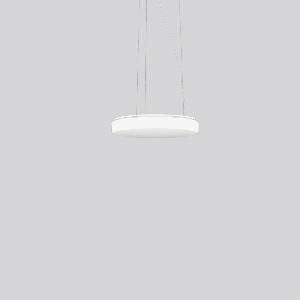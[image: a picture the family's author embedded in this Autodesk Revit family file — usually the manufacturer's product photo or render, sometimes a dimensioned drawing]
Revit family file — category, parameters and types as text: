
# Revit family: flat_polymero_kreis_slim_312089_002_4_338b
name_source: partatom
category: Lighting Fixtures
units: mm (PartAtom-declared; Revit-internal decimal feet)

## family parameters
Cut with Voids When Loaded = No
Host = Face
Light Source = No
Part Type = Normal
Room Calculation Point = No
Round Connector Dimension = Use Diameter
Shared = No

## types (1)
- FLAT POLYMERO KREIS SLIM (1 x LED Modul 840, 2050 lm, 4000)
    Apparent Load = 19 VA
    CIE Flux Codes = 43 74 93 89 100
    Color Rendering = 80
    Color Temperature = 4000
    Default Elevation = 1800 mm
    Description = Series: FLAT POLYMERO KREIS SLIM
Decorative round LED pendant luminaire. Base and canopy: metal, powder-coated, white. Canopy Ø 205 mm, h 35 mm. Diffuser made of plastic (polycarbonate), opal, shockproof. Diffuser fastening: patented push system. Homogeneous and smooth light distribution. Suitable for pendant. 3-point steel cable suspension, steplessly adjustable. Special lengths available on request. 
Colour: white
Diameter: 360 mm
Height: 61 mm
Suspension length: 200-1300 mm
Lamp: LED
Socket: without socket
Colour temperature: 4000K
Colour rendering index (CRI): 83
System power: 19 W
Rated luminous flux: 2050 lm
Luminous efficiency: 108 lm/W
Control gear: AC Strom, dim.Ph.an-/abschnitt
Protection class: I
Type of protection: IP 40
    Height = 61 mm
    Lamp = 1 x LED Modul 840
    Lamp Light Flux = 2050 lm
    Lamp count = 1
    Length = 360 mm
    Lifetime = 50000 h
    Luminous efficacy = 108 lm/W
    Manufacturer = RZB
    ModVariant = No
    Model = 312089.002.4
    Mounting Place = Ceiling
    Mounting Type = Pendant
    Number of Poles = 1
    OnlyDefault = Yes
    Power Factor = 1
    Product Name = FLAT POLYMERO KREIS SLIM
    Product group = Pendant luminaires
    ProductGroupID = 902
    Protection Class = Protection class I
    Protection Degree = IP 40
    RLX_Detail_Level = 1
    RLX_Emergency_Light_Flux = 0 lm
    RLX_Emergency_Type = 0
    RLX_Emergency_Type_DB = No
    RlxData = <blob elided: 57629 chars, md5=49c3c646>
    Socket = socket
    Standby Power = 0 W
    System Light Flux = 2050 lm
    System Power = 19 W
    Type Comments = Product without accessories
    Type Image = 312089.002.jpg
    URL = http://relux.com
    VarID = ---
    Voltage = 230 V
    Voltage Range = 220-240 V
    Weight = 0.00 kg
    Width = 0 mm  [stored 0 ft]

note: [stored X ft] marks values corroborated as IEEE doubles in the binary element streams (Revit-internal decimal feet)

## geometry (parser evidence)
native form markers: Blend x4, Sweep x13
no freeform markers — native parametric forms only
